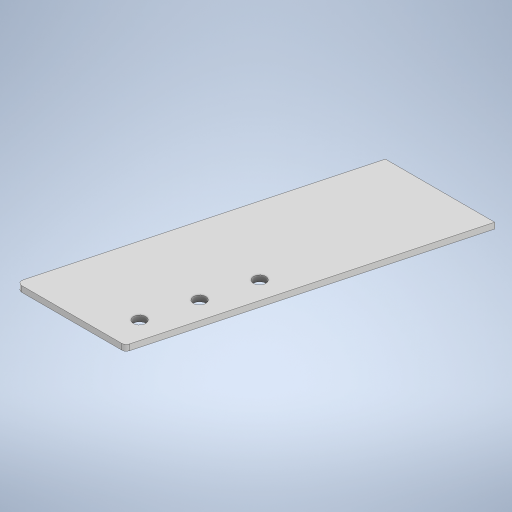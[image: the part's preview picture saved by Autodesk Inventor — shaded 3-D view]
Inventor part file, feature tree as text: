
AUTODESK INVENTOR PART (.ipt)
format: ipt  version: 2024.2 (Build 282272000, 272)  size: 255,488 bytes
history: native  units: mm
features: sketch x2, sheet_metal_op x1, hole x1, chamfer x1, other x1, projected_geometry x1
ambient origin geometry x8: Origin, YZ Plane, XZ Plane, XY Plane, X Axis, Y Axis, Z Axis, Center Point
bodies: Solid1 (feature_tree)
feature tree (7):
  sheet_metal_op  "Face1"
  hole  "Hole1"  [1 undecoded]
  chamfer  "Corner Round1"
  sketch  "Sketch1"  dims[d0=300.0mm d1=200.0mm]
  other  "Plate1"
  sketch  "Sketch3"  dims[d2=15.0deg d3=8.0mm d4=17.0mm d5=6.0mm d6=4.0mm d7=2.0mm d8=90.0deg d9=8.0mm d10=20.594885mm d13=40.0mm d14=6.0mm d25=200.0mm d26=30.0mm d27=30.0mm]
  projected_geometry  "Projected Loop1"
note: 1 required parameter value undecoded (feature->parameter linkage not recoverable at this tier; creation-order binding heuristic only, values carry confidence <= 0.55)
